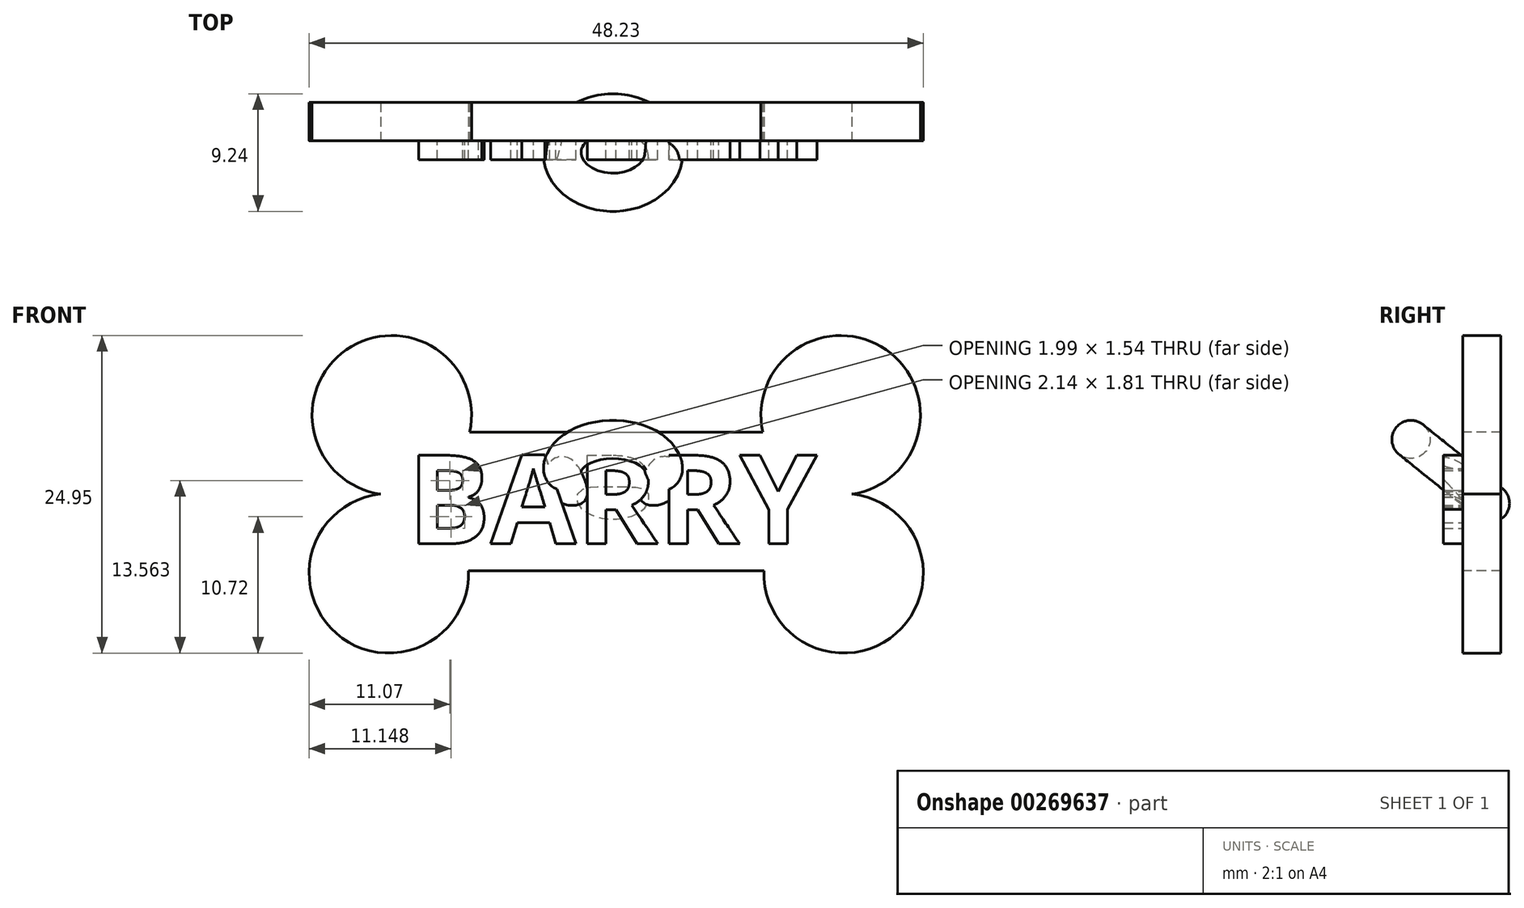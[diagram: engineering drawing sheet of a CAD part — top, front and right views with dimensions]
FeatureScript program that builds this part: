
annotation { "Feature Type Name" : "Feature", "Feature Type Description" : "" }
export const myFeature = defineFeature(function(context is Context, id is Id, definition is map)
    precondition{}
    {
        {
            var Q0;
            Q0=qCreatedBy(makeId("Front.planeOp"),FACE);
            var sketch = newSketch(context, id + "F0", { "sketchPlane" : qUnion([Q0])});
            skText(sketch, "E0", { "text": "BARRY", "fontName": "OpenSans-Bold.ttf"});
            const initialGuessF0  = {"E0": [-0.01809, -0.003, 1, 0, 0.007]};
            skSetInitialGuess(sketch, initialGuessF0);
            skSolve(sketch);
        }
        {
            var Q0;
            Q0=qCreatedBy(makeId("Front.planeOp"),FACE);
            var sketch = newSketch(context, id + "F1", { "sketchPlane" : qUnion([Q0])});
            skLineSegment(sketch, "E1.bottom", {"start": v(-13.2, 5.76) * mm, "end": v(9.8, 5.76) * mm});
            skLineSegment(sketch, "E1.top", {"start": v(-13.3, -5.13) * mm, "end": v(9.9, -5.13) * mm});
            skArc(sketch, "E2", {"start": v(16.8, 0.9) * mm, "mid": v(19.5, 12.23) * mm, "end": v(9.8, 5.76) * mm});
            skArc(sketch, "E3", {"start": v(9.9, -5.13) * mm, "mid": v(20.27, -10.06) * mm, "end": v(16.8, 0.9) * mm});
            skArc(sketch, "E4.MirrorCS", {"start": v(-20.2, 0.9) * mm, "mid": v(-22.9, 12.23) * mm, "end": v(-13.2, 5.76) * mm});
            skArc(sketch, "E5.MirrorCS", {"start": v(-13.3, -5.13) * mm, "mid": v(-23.67, -10.06) * mm, "end": v(-20.2, 0.9) * mm});
            skPoint(sketch, "E6.orphan", {"position": v(-18.67, 0.86) * mm});
            skSolve(sketch);
        }
        {
            var Q0;
            Q0 = qSketchRegion(id + "F1", true);
            extrude(context, id + "F2", {"entities" : qUnion([Q0]), "oppositeDirection" : true, "depth" : 3 * mm});
        }
        {
            var Q0;
            Q0 = qSketchRegion(id + "F0", true);
            extrude(context, id + "F3", {"entities" : qUnion([Q0]), "depth" : 1.5 * mm});
        }
        {
            var Q0;
            Q0=sQuery(id+"F1.wireOp",VERTEX,"E4.MirrorCS.end");
            var Q1;
            Q1=makeQuery(id+"F2.opExtrude","CAP_VERTEX",VERTEX,{"disambiguationData":[OSD([sQuery(id+"F1.wireOp",EDGE,"E1.bottom"),sQuery(id+"F1.wireOp",EDGE,"E4.MirrorCS")])],"isStart":false});
            var Q2;
            Q2=sQuery(id+"F1.wireOp",VERTEX,"E2.end");
            cPlane(context, id + "F4", {"entities" : qUnion([Q0, Q1, Q2]), "cplaneType" : CPlaneType.THREE_POINT, "offset" : 5.76 * mm, "width" : 150 * mm, "height" : 150 * mm});
        }
        {
            var Q0;
            Q0=qCreatedBy(id+"F4.planeOp",FACE);
            var sketch = newSketch(context, id + "F5", { "sketchPlane" : qUnion([Q0])});
            skLineSegment(sketch, "E7", {"start": v(-13.2, 0) * mm, "end": v(-1.7, 0) * mm});
            skLineSegment(sketch, "E8", {"start": v(-1.7, 0) * mm, "end": v(-1.7, 3) * mm, "construction": true});
            skCircle(sketch, "E9", {"center": v(2.3, 1.5) * mm, "radius": 1.5 * mm});
            skLineSegment(sketch, "E10", {"start": v(-1.7, 1.5) * mm, "end": v(2.3, 1.5) * mm});
            skPoint(sketch, "E10.endSnap0", {"position": v(-1.7, 1.5) * mm});
            skSolve(sketch);
        }
        {
            var Q0;
            Q0 = qSketchRegion(id + "F5", true);
            var Q1;
            Q1=sQuery(id+"F5.wireOp",EDGE,"E8");
            revolve(context, id + "F6", {"operationType" : NewBodyOperationType.ADD, "entities" : qUnion([Q0]), "axis" : qUnion([Q1]), "revolveType" : RevolveType.FULL});
        }
    });
